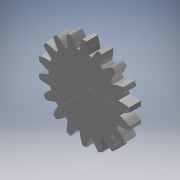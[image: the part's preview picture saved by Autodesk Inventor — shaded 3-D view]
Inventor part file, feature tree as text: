
AUTODESK INVENTOR PART (.ipt)
format: ipt  version: 2017 (Build 210142000, 142)  size: 213,504 bytes
history: native  units: mm (DEFAULTED — no unit token found)
features: plane x3, other x3, sketch x2, extrude x1
ambient origin geometry x8: Origin, YZ Plane, XZ Plane, XY Plane, X Axis, Y Axis, Z Axis, Center Point
bodies: Solid1 (feature_tree)
feature tree (9):
  extrude  "Extrusion1"  Depth=6.35mm TaperAngle=0.0deg
  plane  "Work Plane1"
  plane  "Work Plane2"
  plane  "Work Plane3"
  other  "Spur Gear"
  sketch  "Sketch1"  dims[d0=50.8mm d1=6.35mm d2=0.0mm]
  sketch  "Sketch2"  dims[d3=45.72mm d4=76.2mm d5=0.0mm d6=0.0mm d7=1.745329mm d9=0.0mm d14=0.0mm d15=175.26mm d16=0.0mm d17=0.0mm d18=0.0mm d19=175.26mm]
  other  "Srf1"
  other  "Pitch Diameter"
